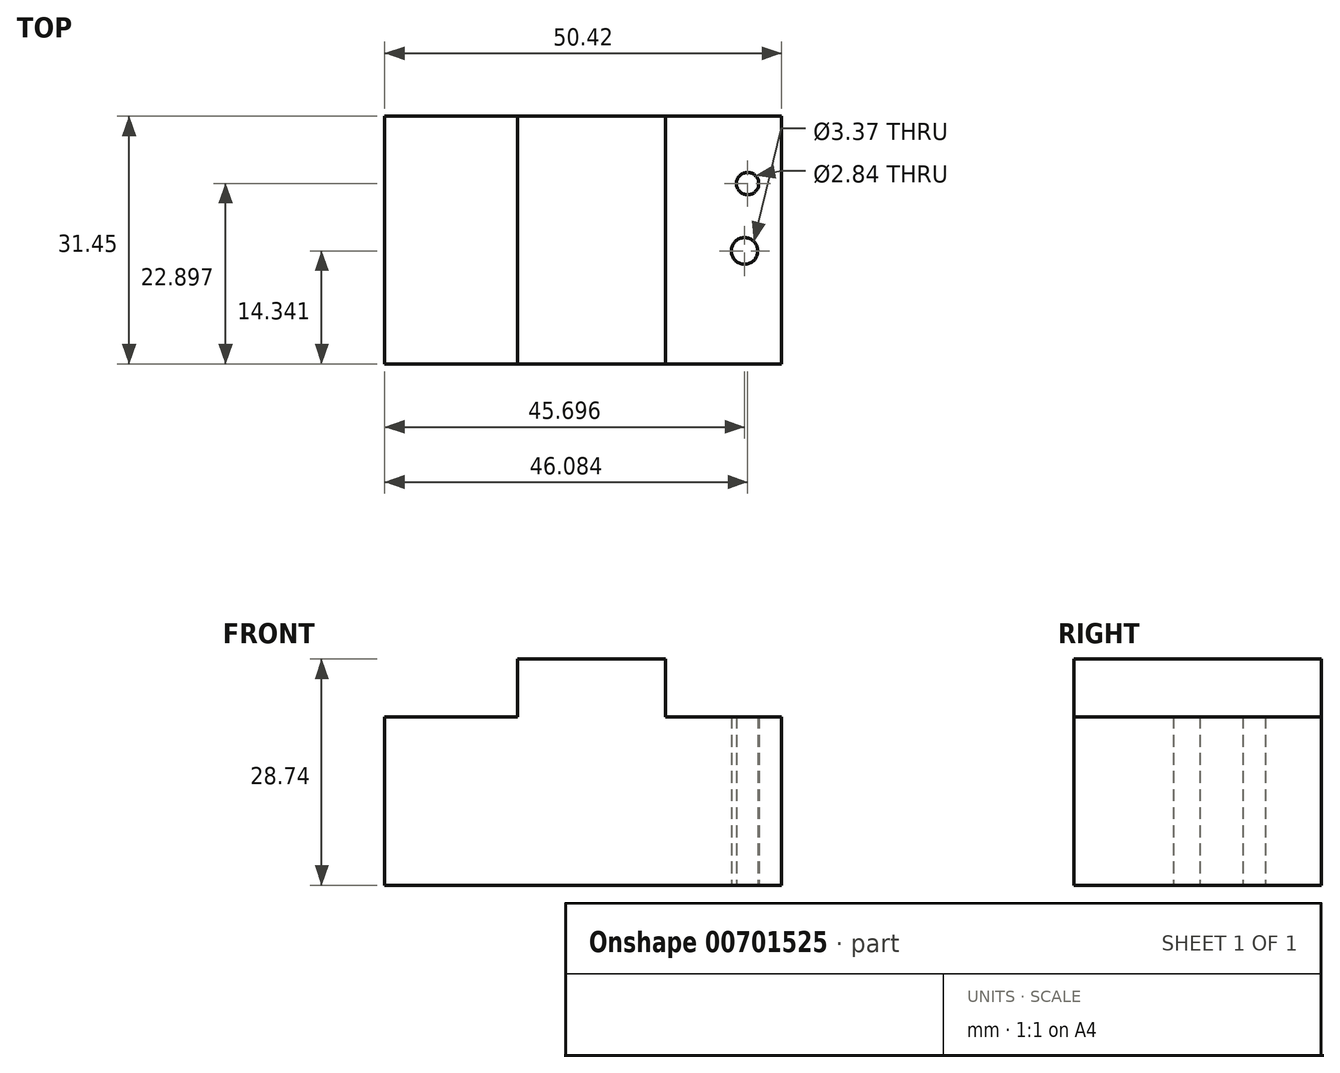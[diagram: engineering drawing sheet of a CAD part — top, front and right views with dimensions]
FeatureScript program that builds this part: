
annotation { "Feature Type Name" : "Feature", "Feature Type Description" : "" }
export const myFeature = defineFeature(function(context is Context, id is Id, definition is map)
    precondition{}
    {
        {
            var Q0;
            Q0=qCreatedBy(makeId("Front.planeOp"),FACE);
            var sketch = newSketch(context, id + "F0", { "sketchPlane" : qUnion([Q0])});
            skLineSegment(sketch, "E0.bottom", {"start": v(-25.21, 10.7) * mm, "end": v(-8.36, 10.7) * mm});
            skLineSegment(sketch, "E0.top", {"start": v(-25.21, -10.7) * mm, "end": v(25.21, -10.7) * mm});
            skLineSegment(sketch, "E0.left", {"start": v(-25.21, 10.7) * mm, "end": v(-25.21, -10.7) * mm});
            skLineSegment(sketch, "E0.right", {"start": v(25.21, 10.7) * mm, "end": v(25.21, -10.7) * mm});
            skPoint(sketch, "E0.middle", {"position": v(0, 0) * mm});
            skLineSegment(sketch, "E1.top", {"start": v(-8.36, 18.04) * mm, "end": v(10.43, 18.04) * mm});
            skLineSegment(sketch, "E1.left", {"start": v(-8.36, 10.7) * mm, "end": v(-8.36, 18.04) * mm});
            skLineSegment(sketch, "E1.right", {"start": v(10.43, 10.7) * mm, "end": v(10.43, 18.04) * mm});
            skLineSegment(sketch, "E2.trimOffspring", {"start": v(10.43, 10.7) * mm, "end": v(25.21, 10.7) * mm});
            skSolve(sketch);
        }
        {
            var Q0;
            Q0=makeQuery(id+"F0.imprint","IMPRINT",FACE,{"disambiguationData":[TD([[makeQuery(id+"F0.imprint","IMPRINT",EDGE,{"derivedFrom":sQuery(id+"F0.wireOp",EDGE,"E0.bottom")}),-1.0]])]});
            extrude(context, id + "F1", {"entities" : qUnion([Q0]), "oppositeDirection" : true, "depth" : 31.45 * mm, "offsetDistance" : 25.4 * mm});
        }
        {
            var Q0;
            Q0=makeQuery(id+"F1.opExtrude","SWEPT_FACE",FACE,{"disambiguationData":[OSD([sQuery(id+"F0.wireOp",EDGE,"E0.top")])]});
            var sketch = newSketch(context, id + "F2", { "sketchPlane" : qUnion([Q0])});
            skSolve(sketch);
        }
        {
            var Q0;
            {var subQ0=sQuery(id+"F0.wireOp",EDGE,"E0.top");Q0=makeQuery(id+"F2.imprint","IMPRINT",FACE,{"disambiguationData":[TD([[makeQuery(id+"F2.imprint","IMPRINT",EDGE,{"derivedFrom":makeQuery(id+"F1.opExtrude","CAP_EDGE",EDGE,{"disambiguationData":[OSD([subQ0])],"isStart":true})}),-1.0]])]});}
            var sketch = newSketch(context, id + "F3", { "sketchPlane" : qUnion([Q0])});
            skCircle(sketch, "E3", {"center": v(20.49, -14.34) * mm, "radius": 1.69 * mm});
            skCircle(sketch, "E4", {"center": v(20.87, -22.9) * mm, "radius": 1.42 * mm});
            skSolve(sketch);
        }
        {
            var Q0;
            Q0=makeQuery(id+"F3.imprint","IMPRINT",FACE,{"disambiguationData":[TD([[makeQuery(id+"F3.imprint","IMPRINT",EDGE,{"derivedFrom":sQuery(id+"F3.wireOp",EDGE,"E3")}),1.0]])]});
            extrude(context, id + "F4", {"entities" : qUnion([Q0]), "operationType" : NewBodyOperationType.REMOVE, "oppositeDirection" : true, "depth" : 25.4 * mm, "offsetDistance" : 25.4 * mm});
        }
        {
            var Q0;
            Q0=makeQuery(id+"F3.imprint","IMPRINT",FACE,{"disambiguationData":[TD([[makeQuery(id+"F3.imprint","IMPRINT",EDGE,{"derivedFrom":sQuery(id+"F3.wireOp",EDGE,"E4")}),1.0]])]});
            extrude(context, id + "F5", {"entities" : qUnion([Q0]), "operationType" : NewBodyOperationType.REMOVE, "oppositeDirection" : true, "depth" : 25.4 * mm, "offsetDistance" : 25.4 * mm});
        }
    });
